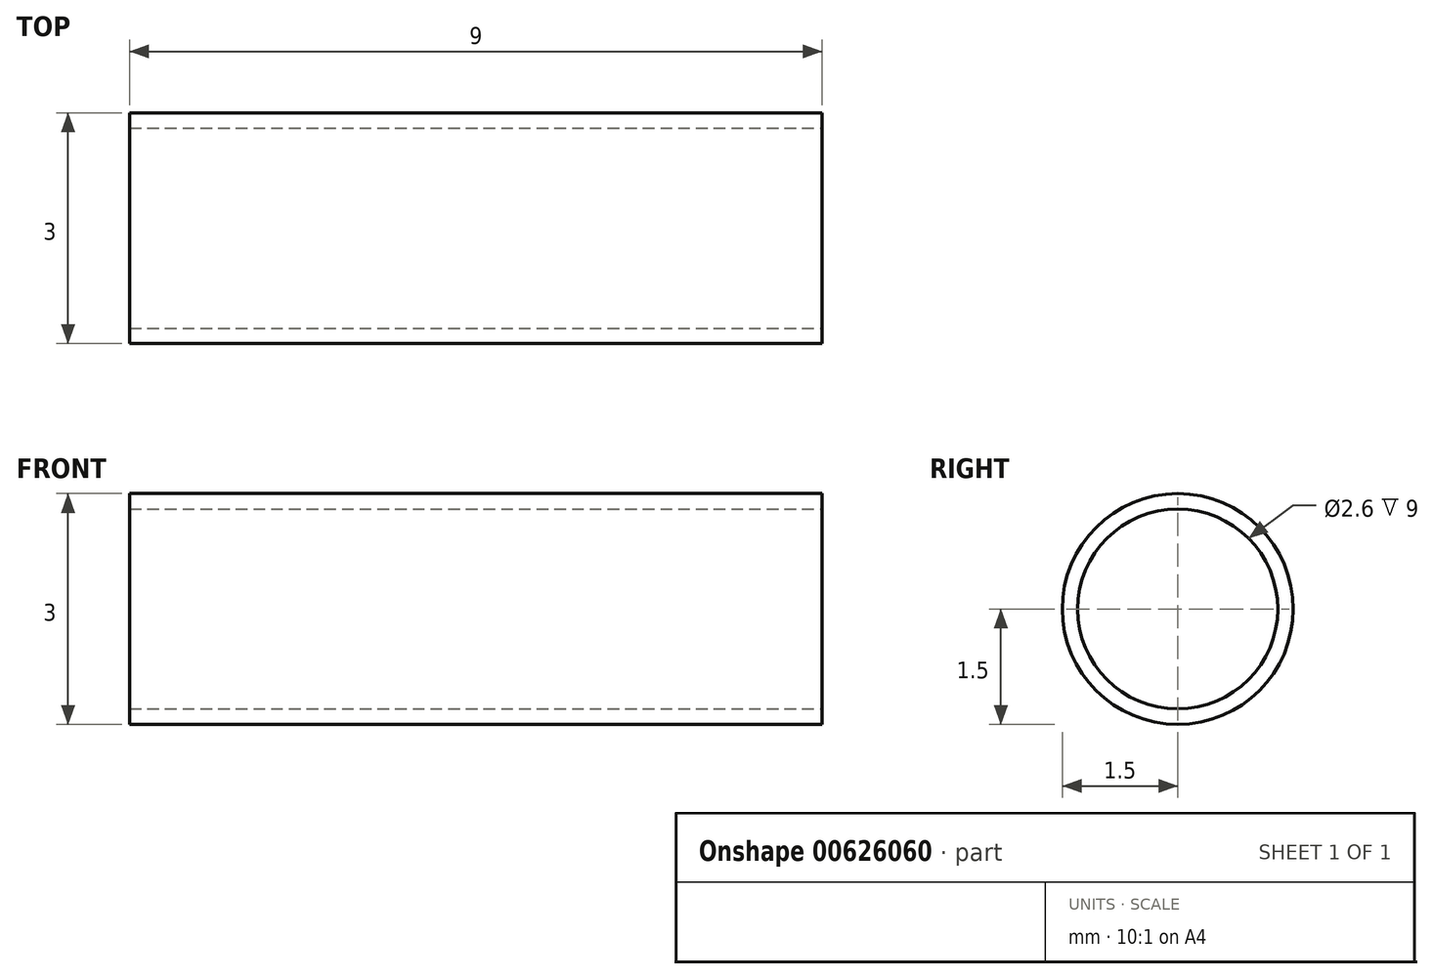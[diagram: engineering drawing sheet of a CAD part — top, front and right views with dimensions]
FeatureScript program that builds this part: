
annotation { "Feature Type Name" : "Feature", "Feature Type Description" : "" }
export const myFeature = defineFeature(function(context is Context, id is Id, definition is map)
    precondition{}
    {
        {
            var Q0;
            Q0=qCreatedBy(makeId("Front.planeOp"),FACE);
            var sketch = newSketch(context, id + "F0", { "sketchPlane" : qUnion([Q0])});
            skLineSegment(sketch, "E0.bottom", {"start": v(0, 0) * mm, "end": v(9, 0) * mm});
            skLineSegment(sketch, "E0.top", {"start": v(0, 1.5) * mm, "end": v(9, 1.5) * mm});
            skLineSegment(sketch, "E0.left", {"start": v(0, 0) * mm, "end": v(0, 1.5) * mm});
            skLineSegment(sketch, "E0.right", {"start": v(9, 0) * mm, "end": v(9, 1.5) * mm});
            skSolve(sketch);
        }
        {
            var Q0;
            Q0=makeQuery(id+"F0.imprint","IMPRINT",FACE,{"disambiguationData":[TD([[makeQuery(id+"F0.imprint","IMPRINT",EDGE,{"derivedFrom":sQuery(id+"F0.wireOp",EDGE,"E0.bottom")}),1.0]])]});
            var Q1;
            Q1=sQuery(id+"F0.wireOp",EDGE,"E0.bottom");
            revolve(context, id + "F1", {"entities" : qUnion([Q0]), "axis" : qUnion([Q1]), "revolveType" : RevolveType.FULL});
        }
        {
            var Q0;
            Q0=makeQuery(id+"F1.opRevolve","SWEPT_FACE",FACE,{"disambiguationData":[OSD([sQuery(id+"F0.wireOp",EDGE,"E0.right")])]});
            var sketch = newSketch(context, id + "F2", { "sketchPlane" : qUnion([Q0])});
            skCircle(sketch, "E1", {"center": v(0, 0) * mm, "radius": 1.3 * mm});
            skSolve(sketch);
        }
        {
            var Q0;
            Q0=makeQuery(id+"F2.imprint","IMPRINT",FACE,{"disambiguationData":[TD([[makeQuery(id+"F2.imprint","IMPRINT",EDGE,{"derivedFrom":sQuery(id+"F2.wireOp",EDGE,"E1")}),1.0]])]});
            extrude(context, id + "F3", {"entities" : qUnion([Q0]), "operationType" : NewBodyOperationType.REMOVE, "oppositeDirection" : true, "depth" : 25 * mm, "offsetDistance" : 25 * mm});
        }
    });
